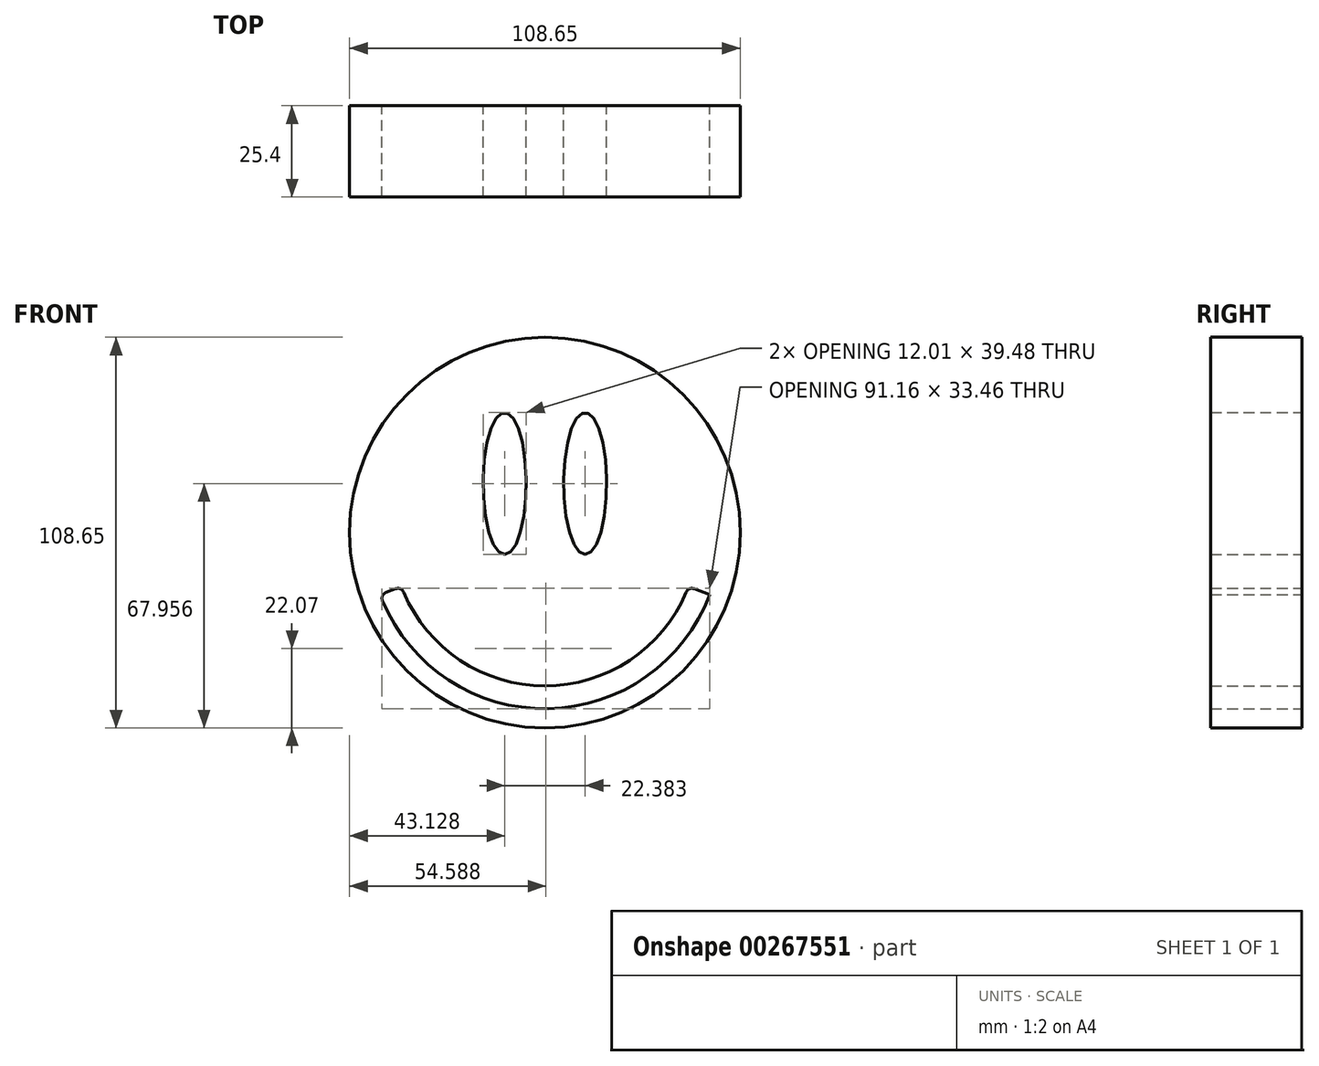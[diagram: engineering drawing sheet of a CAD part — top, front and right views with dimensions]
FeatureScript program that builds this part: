
annotation { "Feature Type Name" : "Feature", "Feature Type Description" : "" }
export const myFeature = defineFeature(function(context is Context, id is Id, definition is map)
    precondition{}
    {
        {
            var Q0;
            Q0=qCreatedBy(makeId("Front.planeOp"),FACE);
            var sketch = newSketch(context, id + "F0", { "sketchPlane" : qUnion([Q0])});
            skCircle(sketch, "E0", {"center": v(-8.75, 11.8) * mm, "radius": 54.33 * mm});
            skEllipse(sketch, "E1", {"center": v(-19.94, 25.44) * mm, "majorRadius": 19.74 * mm, "minorRadius": 6 * mm, "majorAxis": v(0, -1)});
            skEllipse(sketch, "E2.MirrorC", {"center": v(2.44, 25.44) * mm, "majorRadius": 19.74 * mm, "minorRadius": 6 * mm, "majorAxis": v(0, -1)});
            skArc(sketch, "E3.0", {"start": v(-53.93, -7.15) * mm, "mid": v(-7.84, -37.18) * mm, "end": v(37.1, -5.47) * mm});
            skArc(sketch, "E4.0", {"start": v(-48.03, -4.78) * mm, "mid": v(-8.75, -30.84) * mm, "end": v(30.54, -4.78) * mm});
            skLineSegment(sketch, "E5", {"start": v(-52.93, -4.84) * mm, "end": v(-50.25, -3.83) * mm});
            skLineSegment(sketch, "E6", {"start": v(32.76, -3.83) * mm, "end": v(37.1, -5.47) * mm});
            skPoint(sketch, "E7.visualSharp", {"position": v(-54.6, -5.47) * mm});
            skArc(sketch, "E7.filletArc", {"start": v(-52.93, -4.84) * mm, "mid": v(-53.92, -5.78) * mm, "end": v(-53.93, -7.15) * mm});
            skPoint(sketch, "E8.visualSharp", {"position": v(-48.65, -3.23) * mm});
            skArc(sketch, "E8.filletArc", {"start": v(-48.03, -4.78) * mm, "mid": v(-48.95, -3.86) * mm, "end": v(-50.25, -3.83) * mm});
            skPoint(sketch, "E9.visualSharp", {"position": v(31.16, -3.23) * mm});
            skArc(sketch, "E9.filletArc", {"start": v(32.76, -3.83) * mm, "mid": v(31.45, -3.86) * mm, "end": v(30.54, -4.78) * mm});
            skSolve(sketch);
        }
        {
            var Q0;
            Q0=makeQuery(id+"F0.imprint","IMPRINT",FACE,{"disambiguationData":[TD([[makeQuery(id+"F0.imprint","IMPRINT",EDGE,{"derivedFrom":sQuery(id+"F0.wireOp",EDGE,"E0")}),1.0]])]});
            extrude(context, id + "F1", {"entities" : qUnion([Q0]), "depth" : 25.4 * mm});
        }
    });
